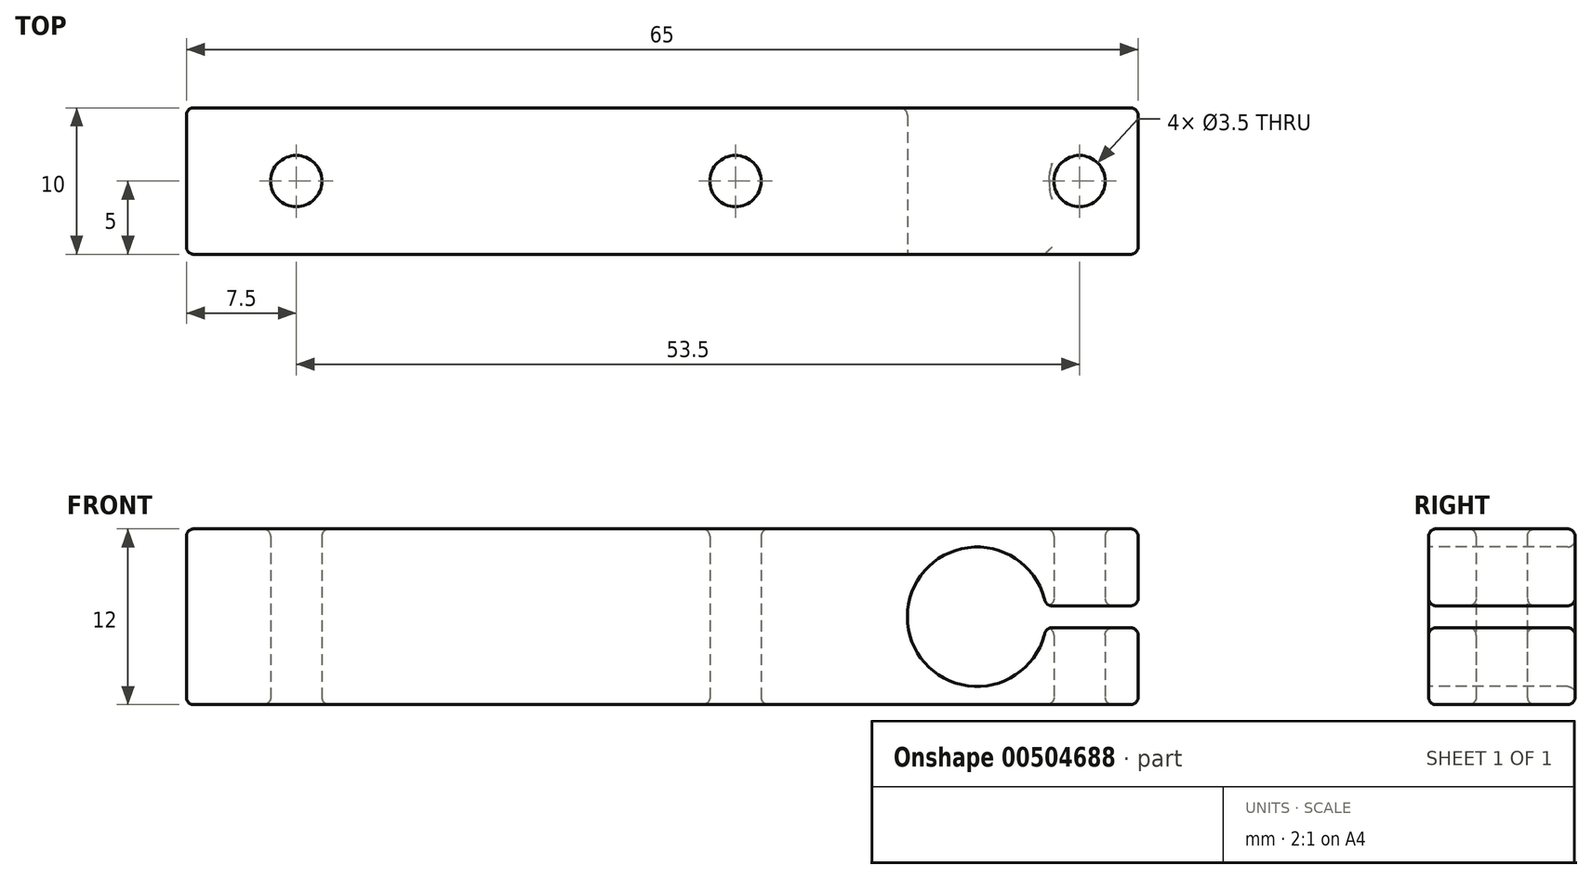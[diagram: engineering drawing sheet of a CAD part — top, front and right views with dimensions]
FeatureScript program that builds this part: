
annotation { "Feature Type Name" : "Feature", "Feature Type Description" : "" }
export const myFeature = defineFeature(function(context is Context, id is Id, definition is map)
    precondition{}
    {
        {
            var Q0;
            Q0=qCreatedBy(makeId("Top.planeOp"),FACE);
            var sketch = newSketch(context, id + "F0", { "sketchPlane" : qUnion([Q0])});
            skLineSegment(sketch, "E0.bottom", {"start": v(42.5, 5) * mm, "end": v(-22.5, 5) * mm});
            skLineSegment(sketch, "E0.top", {"start": v(42.5, -5) * mm, "end": v(-22.5, -5) * mm});
            skLineSegment(sketch, "E0.left", {"start": v(42.5, 5) * mm, "end": v(42.5, -5) * mm});
            skLineSegment(sketch, "E0.right", {"start": v(-22.5, 5) * mm, "end": v(-22.5, -5) * mm});
            skPoint(sketch, "E0.middle", {"position": v(0, 0) * mm});
            skCircle(sketch, "E1", {"center": v(-15, 0) * mm, "radius": 1.75 * mm});
            skCircle(sketch, "E2", {"center": v(15, 0) * mm, "radius": 1.75 * mm});
            skCircle(sketch, "E3", {"center": v(38.5, 0) * mm, "radius": 1.75 * mm});
            skSolve(sketch);
        }
        {
            var Q0;
            Q0=makeQuery(id+"F0.imprint","IMPRINT",FACE,{"disambiguationData":[TD([[makeQuery(id+"F0.imprint","IMPRINT",EDGE,{"derivedFrom":sQuery(id+"F0.wireOp",EDGE,"E0.bottom")}),1.0]])]});
            extrude(context, id + "F1", {"entities" : qUnion([Q0]), "depth" : 12 * mm});
        }
        {
            var Q0;
            Q0=makeQuery(id+"F1.opExtrude","SWEPT_FACE",FACE,{"disambiguationData":[OSD([sQuery(id+"F0.wireOp",EDGE,"E0.top")])]});
            var sketch = newSketch(context, id + "F2", { "sketchPlane" : qUnion([Q0])});
            skPoint(sketch, "E4.centerSnap0", {"position": v(42.5, 6) * mm});
            skLineSegment(sketch, "E5", {"start": v(42.5, 6.75) * mm, "end": v(36.2, 6.75) * mm});
            skLineSegment(sketch, "E6", {"start": v(36.2, 5.25) * mm, "end": v(42.5, 5.25) * mm});
            skLineSegment(sketch, "E7", {"start": v(42.5, 6.75) * mm, "end": v(42.5, 5.25) * mm});
            skArc(sketch, "E8", {"start": v(36.2, 6.75) * mm, "mid": v(26.74, 6) * mm, "end": v(36.2, 5.25) * mm});
            skLineSegment(sketch, "E9", {"start": v(42.5, 6) * mm, "end": v(40.18, 6) * mm, "construction": true});
            skSolve(sketch);
        }
        {
            var Q0;
            Q0 = qSketchRegion(id + "F2", true);
            extrude(context, id + "F3", {"entities" : qUnion([Q0]), "operationType" : NewBodyOperationType.REMOVE, "endBound" : BoundingType.THROUGH_ALL, "oppositeDirection" : true, "depth" : 25 * mm});
        }
        {
            var Q0;
            Q0=makeQuery(id+"F1.opExtrude","CAP_FACE",FACE,{"disambiguationData":[OSD([sQuery(id+"F0.wireOp",EDGE,"E0.bottom"),sQuery(id+"F0.wireOp",EDGE,"E0.top"),sQuery(id+"F0.wireOp",EDGE,"E0.left"),sQuery(id+"F0.wireOp",EDGE,"E0.right"),sQuery(id+"F0.wireOp",EDGE,"E1"),sQuery(id+"F0.wireOp",EDGE,"E2"),sQuery(id+"F0.wireOp",EDGE,"E3")])],"isStart":false});
            var Q1;
            Q1=makeQuery(id+"F1.opExtrude","SWEPT_FACE",FACE,{"disambiguationData":[OSD([sQuery(id+"F0.wireOp",EDGE,"E0.bottom")])]});
            var Q2;
            {var subQ1=sQuery(id+"F0.wireOp",EDGE,"E0.left");Q2=makeQuery(id+"F3.boolean.opBoolean","SPLIT",FACE,{"disambiguationData":[TD([makeQuery(id+"F3.opExtrude","SWEPT_FACE",FACE,{"disambiguationData":[OSD([sQuery(id+"F2.wireOp",EDGE,"E6")])]})])],"derivedFrom":makeQuery(id+"F1.opExtrude","SWEPT_FACE",FACE,{"disambiguationData":[OSD([subQ1])]})});}
            var Q3;
            {var subQ1=sQuery(id+"F0.wireOp",EDGE,"E0.left");Q3=makeQuery(id+"F3.boolean.opBoolean","SPLIT",FACE,{"disambiguationData":[TD([makeQuery(id+"F3.opExtrude","SWEPT_FACE",FACE,{"disambiguationData":[OSD([sQuery(id+"F2.wireOp",EDGE,"E5")])]})])],"derivedFrom":makeQuery(id+"F1.opExtrude","SWEPT_FACE",FACE,{"disambiguationData":[OSD([subQ1])]})});}
            var Q4;
            Q4=makeQuery(id+"F1.opExtrude","SWEPT_FACE",FACE,{"disambiguationData":[OSD([sQuery(id+"F0.wireOp",EDGE,"E0.right")])]});
            var Q5;
            Q5=makeQuery(id+"F1.opExtrude","CAP_FACE",FACE,{"disambiguationData":[OSD([sQuery(id+"F0.wireOp",EDGE,"E0.bottom"),sQuery(id+"F0.wireOp",EDGE,"E0.top"),sQuery(id+"F0.wireOp",EDGE,"E0.left"),sQuery(id+"F0.wireOp",EDGE,"E0.right"),sQuery(id+"F0.wireOp",EDGE,"E1"),sQuery(id+"F0.wireOp",EDGE,"E2"),sQuery(id+"F0.wireOp",EDGE,"E3")])],"isStart":true});
            var Q6;
            Q6=makeQuery(id+"F3.boolean.opBoolean","COPY",FACE,{"derivedFrom":makeQuery(id+"F3.opExtrude","SWEPT_FACE",FACE,{"disambiguationData":[OSD([sQuery(id+"F2.wireOp",EDGE,"E6")])]})});
            var Q7;
            Q7=makeQuery(id+"F3.boolean.opBoolean","COPY",FACE,{"derivedFrom":makeQuery(id+"F3.opExtrude","SWEPT_FACE",FACE,{"disambiguationData":[OSD([sQuery(id+"F2.wireOp",EDGE,"E5")])]})});
            fillet(context, id + "F4", {"entities" : qUnion([Q0, Q1, Q2, Q3, Q4, Q5, Q6, Q7]), "radius" : .5 * mm, "tangentPropagation" : true, "allowEdgeOverflow" : false});
        }
    });
